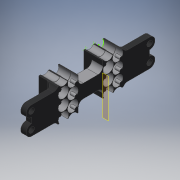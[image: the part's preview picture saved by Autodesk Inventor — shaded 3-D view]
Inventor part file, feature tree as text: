
AUTODESK INVENTOR PART (.ipt)
format: ipt  version: 2016 (Build 200138000, 138)  size: 401,920 bytes
history: native  units: mm
features: extrude x5, sketch x5, other x3, projected_geometry x2, fillet x1, plane x1
ambient origin geometry x8: Origin, YZ Plane, XZ Plane, XY Plane, X Axis, Y Axis, Z Axis, Center Point
bodies: Solid1 (feature_tree)
feature tree (17):
  other  "Main Assembly.iam"
  other  "Motor holder.ipt:1"
  other  "Motor holder.ipt:3"
  extrude  "Extrusion1"  Depth=10.0mm TaperAngle=0.0deg
  extrude  "Extrusion2"  Depth=2.25mm TaperAngle=0.0deg
  extrude  "Extrusion3"  Depth=2.0mm
  fillet  "Fillet1"  Radius=1.2mm
  extrude  "Extrusion4"  Depth=1.2mm
  extrude  "Extrusion5"  Depth=4.2mm
  plane  "Work Plane1"
  sketch  "Sketch2"  dims[d0=10.0mm d1=10.0mm d2=0.0mm]
  sketch  "Sketch4"  dims[d3=2.25mm d4=0.0mm d5=2.25mm d6=0.0mm]
  projected_geometry  "Projected Loop1"
  sketch  "Sketch5"  dims[d7=2.0mm d10=1.2mm d11=1.2mm]
  projected_geometry  "Projected Loop2"
  sketch  "Sketch6"  dims[d12=1.2mm d13=1.2mm]
  sketch  "Sketch7"  dims[d14=2.25mm d15=0.0mm d16=4.2mm d17=4.2mm d18=2.25mm d19=0.0mm]
